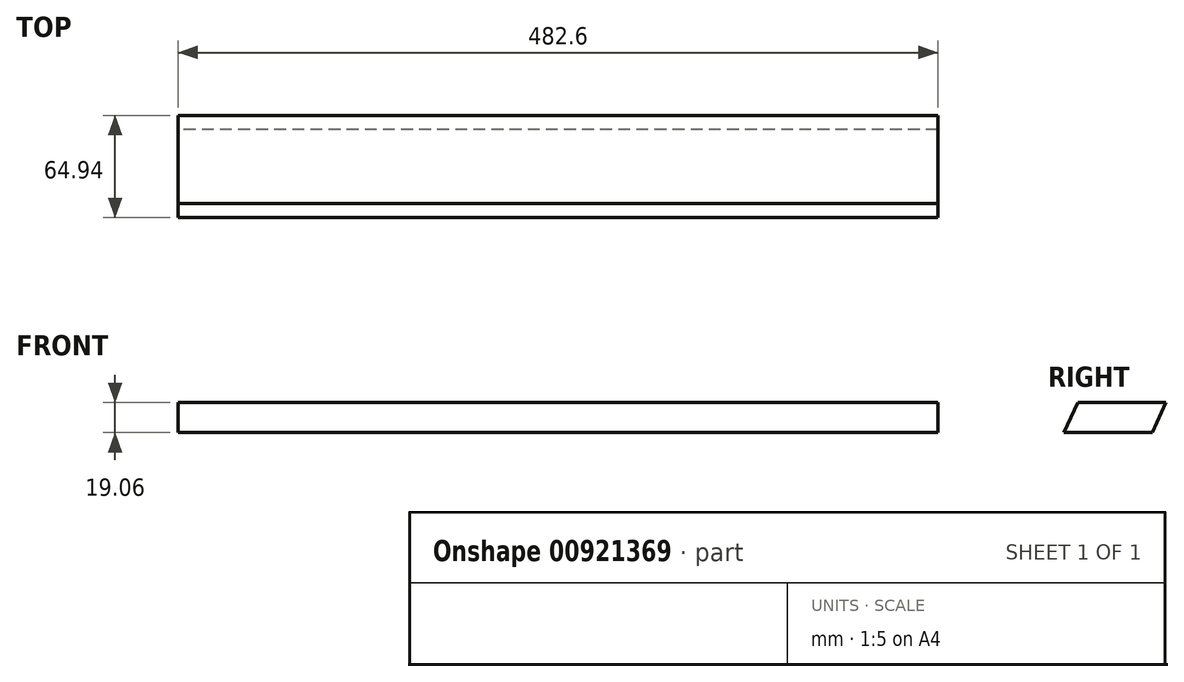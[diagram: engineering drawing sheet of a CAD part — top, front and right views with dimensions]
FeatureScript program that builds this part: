
annotation { "Feature Type Name" : "Feature", "Feature Type Description" : "" }
export const myFeature = defineFeature(function(context is Context, id is Id, definition is map)
    precondition{}
    {
        {
            var Q0;
            Q0=qCreatedBy(makeId("Right.planeOp"),FACE);
            var sketch = newSketch(context, id + "F0", { "sketchPlane" : qUnion([Q0])});
            skLineSegment(sketch, "E0", {"start": v(-32.47, -9.53) * mm, "end": v(-23.58, 9.53) * mm});
            skLineSegment(sketch, "E1", {"start": v(-23.58, 9.53) * mm, "end": v(32.47, 9.53) * mm});
            skLineSegment(sketch, "E2", {"start": v(32.47, 9.53) * mm, "end": v(23.58, -9.52) * mm});
            skLineSegment(sketch, "E3", {"start": v(23.58, -9.52) * mm, "end": v(-32.47, -9.53) * mm});
            skLineSegment(sketch, "E4", {"start": v(-23.58, 9.53) * mm, "end": v(23.58, -9.53) * mm, "construction": true});
            skSolve(sketch);
        }
        {
            var Q0;
            Q0 = qSketchRegion(id + "F0", true);
            extrude(context, id + "F1", {"entities" : qUnion([Q0]), "endBound" : BoundingType.SYMMETRIC, "depth" : 482.6 * mm, "offsetDistance" : 25.4 * mm});
        }
    });
